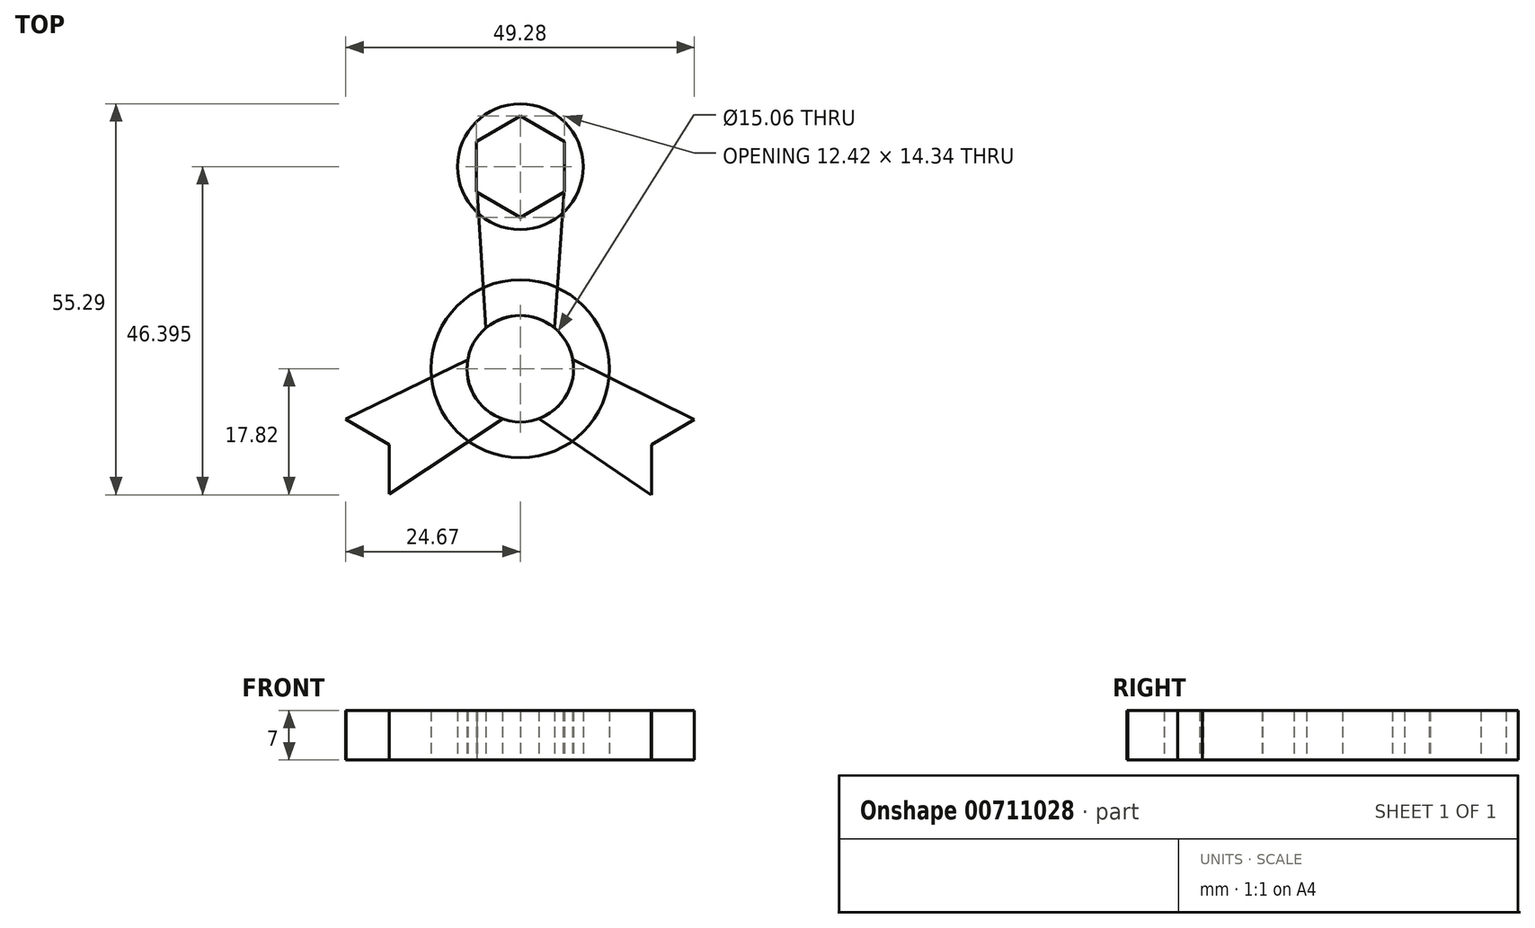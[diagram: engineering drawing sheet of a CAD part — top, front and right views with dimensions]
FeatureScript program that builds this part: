
annotation { "Feature Type Name" : "Feature", "Feature Type Description" : "" }
export const myFeature = defineFeature(function(context is Context, id is Id, definition is map)
    precondition{}
    {
        {
            var Q0;
            Q0=qCreatedBy(makeId("Top.planeOp"),FACE);
            var sketch = newSketch(context, id + "F0", { "sketchPlane" : qUnion([Q0])});
            skCircle(sketch, "E0", {"center": v(0, 0) * mm, "radius": 7.53 * mm});
            skSolve(sketch);
        }
        {
            var Q0;
            Q0 = qSketchRegion(id + "F0", true);
            var sketch = newSketch(context, id + "F1", { "sketchPlane" : qUnion([Q0])});
            skCircle(sketch, "E1", {"center": v(0, 0) * mm, "radius": 12.6 * mm});
            skSolve(sketch);
        }
        {
            var Q0;
            Q0=qCreatedBy(makeId("Top.planeOp"),FACE);
            var sketch = newSketch(context, id + "F2", { "sketchPlane" : qUnion([Q0])});
            skPoint(sketch, "E2", {"position": v(0, 28.58) * mm});
            skCircle(sketch, "E3.cCircle", {"center": v(0, 28.58) * mm, "radius": 6.2 * mm, "construction": true});
            skLineSegment(sketch, "E3.0", {"start": v(6.21, 32.16) * mm, "end": v(6.21, 24.99) * mm});
            skLineSegment(sketch, "E3.1", {"start": v(6.21, 24.99) * mm, "end": v(0, 21.4) * mm});
            skLineSegment(sketch, "E3.2", {"start": v(0, 21.4) * mm, "end": v(-6.21, 24.99) * mm});
            skLineSegment(sketch, "E3.3", {"start": v(-6.21, 24.99) * mm, "end": v(-6.21, 32.16) * mm});
            skLineSegment(sketch, "E3.4", {"start": v(-6.2, 32.16) * mm, "end": v(0, 35.75) * mm});
            skLineSegment(sketch, "E3.5", {"start": v(0, 35.75) * mm, "end": v(6.21, 32.16) * mm});
            skPoint(sketch, "E3.0.midPoint", {"position": v(6.21, 28.58) * mm});
            skSolve(sketch);
        }
        {
            var Q0;
            Q0=qCreatedBy(makeId("Top.planeOp"),FACE);
            var sketch = newSketch(context, id + "F3", { "sketchPlane" : qUnion([Q0])});
            skPoint(sketch, "E4", {"position": v(0, 28.58) * mm});
            skCircle(sketch, "E5", {"center": v(0, 28.58) * mm, "radius": 8.9 * mm});
            skSolve(sketch);
        }
        {
            var Q0;
            Q0=qCreatedBy(makeId("Top.planeOp"),FACE);
            var sketch = newSketch(context, id + "F4", { "sketchPlane" : qUnion([Q0])});
            skLineSegment(sketch, "E6", {"start": v(6.2, 24.9) * mm, "end": v(4.4, 0) * mm});
            skLineSegment(sketch, "E7", {"start": v(4.4, 0) * mm, "end": v(-4.5, 0) * mm});
            skLineSegment(sketch, "E8", {"start": v(-4.5, 0) * mm, "end": v(-6.09, 24.9) * mm});
            skLineSegment(sketch, "E9", {"start": v(-6.09, 24.9) * mm, "end": v(6.2, 24.9) * mm});
            skSolve(sketch);
        }
        {
            var Q0;
            Q0=makeQuery(id+"F3.imprint","IMPRINT",FACE,{"disambiguationData":[TD([[makeQuery(id+"F3.imprint","IMPRINT",EDGE,{"derivedFrom":sQuery(id+"F3.wireOp",EDGE,"E5")}),1.0]])]});
            var Q1;
            Q1=makeQuery(id+"F1.imprint","IMPRINT",FACE,{"disambiguationData":[TD([[makeQuery(id+"F1.imprint","IMPRINT",EDGE,{"derivedFrom":sQuery(id+"F1.wireOp",EDGE,"E1")}),1.0]])]});
            var Q2;
            Q2=makeQuery(id+"F4.imprint","IMPRINT",FACE,{"disambiguationData":[TD([[makeQuery(id+"F4.imprint","IMPRINT",EDGE,{"derivedFrom":sQuery(id+"F4.wireOp",EDGE,"E6")}),-1.0]])]});
            extrude(context, id + "F5", {"entities" : qUnion([Q0, Q1, Q2]), "depth" : 7 * mm, "offsetDistance" : 25.4 * mm});
        }
        {
            var Q0;
            Q0 = qSketchRegion(id + "F2", true);
            extrude(context, id + "F6", {"entities" : qUnion([Q0]), "operationType" : NewBodyOperationType.REMOVE, "depth" : 7 * mm, "offsetDistance" : 25.4 * mm});
        }
        {
            var Q0;
            Q0 = qSketchRegion(id + "F0", true);
            extrude(context, id + "F7", {"entities" : qUnion([Q0]), "operationType" : NewBodyOperationType.REMOVE, "depth" : 7 * mm, "offsetDistance" : 25.4 * mm});
        }
        {
            var Q0;
            Q0=makeQuery(id+"F5.opExtrude","SWEPT_BODY",BODY,{"disambiguationData":[OSD([sQuery(id+"F4.wireOp",EDGE,"E6"),sQuery(id+"F4.wireOp",EDGE,"E7"),sQuery(id+"F4.wireOp",EDGE,"E8"),sQuery(id+"F4.wireOp",EDGE,"E9")])]});
            var Q1;
            {var subQ0=sQuery(id+"F0.wireOp",EDGE,"E0");Q1=makeQuery(id+"F7.boolean.opBoolean","MERGE",EDGE,{"derivedFrom":[makeQuery(id+"F5.opExtrude","CAP_EDGE",EDGE,{"disambiguationData":[OSD([subQ0])],"isStart":false}),makeQuery(id+"F7.opExtrude","CAP_EDGE",EDGE,{"disambiguationData":[OSD([subQ0])],"isStart":false})]});}
            circularPattern(context, id + "F8", {"entities" : qUnion([Q0]), "axis" : qUnion([Q1]), "angle" : 360 * degree, "instanceCount" : 3, "equalSpace" : true});
        }
    });
